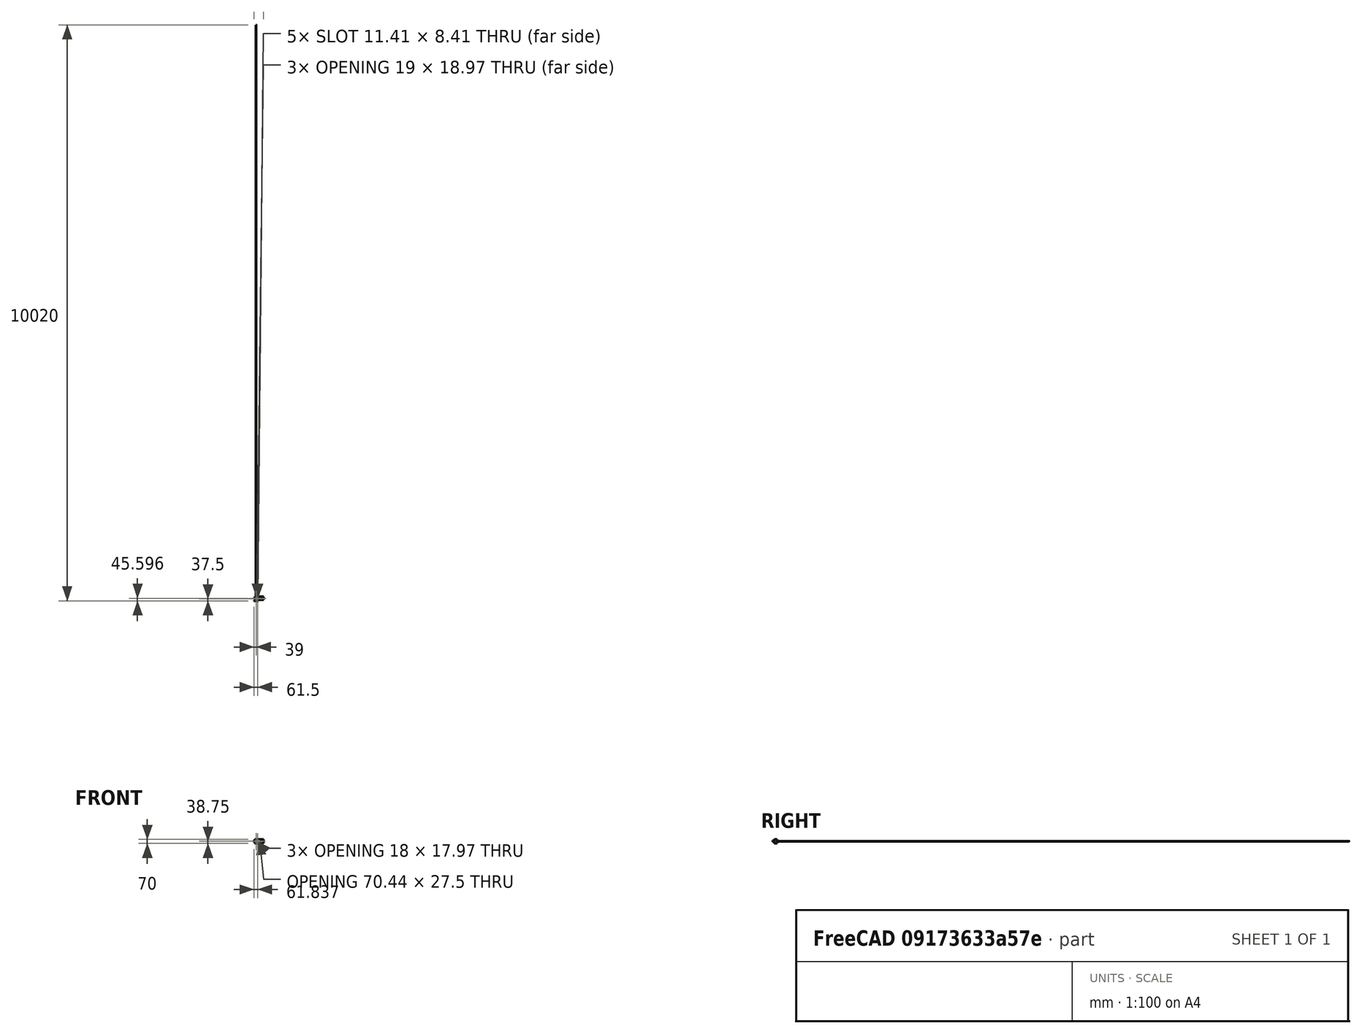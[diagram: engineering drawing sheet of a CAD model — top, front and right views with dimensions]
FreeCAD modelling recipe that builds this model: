
FCSTD DOCUMENT  (FreeCAD 0.16R5861 (Git))
Label: flexystruder_body_holderV0.3
License: CreativeCommons Attribution-ShareAlike
LicenseURL: http://creativecommons.org/licenses/by-sa/4.0/
objects: Sketcher::SketchObject×8, PartDesign::Pad×6, Part::Feature×4, PartDesign::Pocket×2, Mesh::Feature×1, PartDesign::Chamfer×1, Part::Cut×1, PartDesign::Fillet×1
note: 31 computed .brp shape members not serialized (recipe doc carries the construction recipe); baked Part::Feature solids carry a one-line shape summary decoded from their .brp

FEATURE [Mesh::Feature] flexystruder_body_hex_v2_0  label="flexystruder_body_hex_v2.0"
FEATURE [Part::Feature] flexystruder_body_hex_v2_0001
  shape: bbox 97.06 x 64.55 x 27.5 mm, 7934 faces, 0 solids (baked)
FEATURE [Part::Feature] flexystruder_body_hex_v2_0001001  label="flexystruder_body_hex_v2_0002"
  shape: bbox 97.06 x 64.55 x 27.5 mm, 4378 faces, 0 solids (baked)
FEATURE [Part::Feature] flexystruder_body_hex_v2_0001001_solid  label="flexystruder_body_hex_v2_0002 (Solid)"
  shape: bbox 97.06 x 64.55 x 27.5 mm, 4378 faces (baked)
FEATURE [Sketcher::SketchObject] Sketch
  Placement = pos=(0,0,0) rot=(1,0,0;3.14159rad)
  Support = -> flexystruder_body_hex_v2_0001001_solid [Face1922]
  sketch-geometry (17):
    g0: ArcOfCircle CenterX=28 CenterY=-45.596 CenterZ=0 NormalX=0 NormalY=0 NormalZ=1 Radius=4.20615 StartAngle=4.71239 EndAngle=7.85398
    g1: ArcOfCircle CenterX=25 CenterY=-45.596 CenterZ=0 NormalX=0 NormalY=0 NormalZ=1 Radius=4.20615 StartAngle=1.5708 EndAngle=4.71239
    g2: LineSegment StartX=28 StartY=-41.3899 StartZ=0 EndX=25 EndY=-41.3899 EndZ=0
    g3: LineSegment StartX=28 StartY=-49.8022 StartZ=0 EndX=25 EndY=-49.8022 EndZ=0
    g4: ArcOfCircle CenterX=52.7327 CenterY=-58.2604 CenterZ=0 NormalX=0 NormalY=0 NormalZ=1 Radius=4.37439 StartAngle=1.5708 EndAngle=4.71239
    g5: ArcOfCircle CenterX=55.547 CenterY=-58.2604 CenterZ=0 NormalX=0 NormalY=0 NormalZ=1 Radius=4.37439 StartAngle=4.71239 EndAngle=7.85398
    g6: LineSegment StartX=52.7327 StartY=-62.6347 StartZ=0 EndX=55.547 EndY=-62.6347 EndZ=0
    g7: LineSegment StartX=52.7327 StartY=-53.886 StartZ=0 EndX=55.547 EndY=-53.886 EndZ=0
    g8: ArcOfCircle CenterX=41 CenterY=-17.6915 CenterZ=0 NormalX=0 NormalY=0 NormalZ=1 Radius=4.05397 StartAngle=4.71239 EndAngle=7.85398
    g9: ArcOfCircle CenterX=37.752 CenterY=-17.6915 CenterZ=0 NormalX=0 NormalY=0 NormalZ=1 Radius=4.05397 StartAngle=1.5708 EndAngle=4.71239
    g10: LineSegment StartX=41 StartY=-13.6375 StartZ=0 EndX=37.752 EndY=-13.6375 EndZ=0
    g11: LineSegment StartX=41 StartY=-21.7455 StartZ=0 EndX=37.752 EndY=-21.7455 EndZ=0
    g12: LineSegment StartX=23.6875 StartY=-6 StartZ=0 EndX=35.6731 EndY=-6 EndZ=0
    g13: LineSegment StartX=16.4026 StartY=-28 StartZ=0 EndX=28.3058 EndY=-28 EndZ=0
    g14: LineSegment StartX=28.3058 StartY=-28 StartZ=0 EndX=35.6731 EndY=-6 EndZ=0
    g15: LineSegment StartX=16.4026 StartY=-28 StartZ=0 EndX=16.4026 EndY=-12.5849 EndZ=0
    g16: ArcOfCircle CenterX=23.5917 CenterY=-13.2161 CenterZ=0 NormalX=0 NormalY=0 NormalZ=1 Radius=7.21677 StartAngle=1.55753 EndAngle=3.05401
  constraints (26):
    c: Tangent(g0,g3) = 1.5708
    c: Tangent(g0,g2) = -1.5708
    c: Tangent(g2,g1) = -1.5708
    c: Tangent(g3,g1) = 1.5708
    c: Horizontal(g2)
    c: Equal(g0,g1)
    c: Tangent(g4,g7) = 1.5708
    c: Tangent(g4,g6) = -1.5708
    c: Tangent(g6,g5) = -1.5708
    c: Tangent(g7,g5) = 1.5708
    c: Horizontal(g6)
    c: Equal(g4,g5)
    c: Tangent(g8,g11) = 1.5708
    c: Tangent(g8,g10) = -1.5708
    c: Tangent(g10,g9) = -1.5708
    c: Tangent(g11,g9) = 1.5708
    c: Horizontal(g10)
    c: Equal(g8,g9)
    c: Horizontal(g12)
    c: Horizontal(g13)
    c: Coincident(g14,g13)
    c: Coincident(g14,g12)
    c: Coincident(g15,g13)
    c: Vertical(g15)
    c: Coincident(g16,g12)
    c: Coincident(g16,g15)
FEATURE [PartDesign::Pad] Pad
  Length = 9.5
  Length2 = 100
  Reversed = true
  Sketch = -> Sketch
  Type = 0
FEATURE [Sketcher::SketchObject] Sketch001
  ExternalGeometry = -> [Pad]
  Placement = pos=(17.5,0,0) rot=(0.57735,0.57735,0.57735;2.0944rad)
  Support = -> Pad [Face375]
  sketch-geometry (4):
    g0: LineSegment StartX=26.5 StartY=12.5 StartZ=0 EndX=17.6702 EndY=12.5 EndZ=0
    g1: LineSegment StartX=17.6702 StartY=12.5 StartZ=0 EndX=17.6702 EndY=9.5 EndZ=0
    g2: LineSegment StartX=17.6702 StartY=9.5 StartZ=0 EndX=26.5 EndY=9.5 EndZ=0
    g3: LineSegment StartX=26.5 StartY=9.5 StartZ=0 EndX=26.5 EndY=12.5 EndZ=0
  constraints (10):
    c: Coincident(g0,g1)
    c: Coincident(g1,g2)
    c: Coincident(g2,g3)
    c: Coincident(g3,g0)
    c: Horizontal(g0)
    c: Horizontal(g2)
    c: Vertical(g1)
    c: Vertical(g3)
    c: Coincident(g0,g-4)
    c: PointOnObject(g1,g-3)
FEATURE [PartDesign::Pad] Pad001
  Length = 3
  Length2 = 100
  Sketch = -> Sketch001
  Type = 0
FEATURE [PartDesign::Chamfer] Chamfer
  Base = -> Pad001 [Edge1475]
  Size = 2.9
FEATURE [Sketcher::SketchObject] Sketch002
  ExternalGeometry = -> [Chamfer]
  Placement = pos=(0,0,27.5) rot=(0,0,1;0rad)
  Support = -> Chamfer [Face24]
  sketch-geometry (4):
    g0: LineSegment StartX=-6.5 StartY=48.2121 StartZ=0 EndX=-6.5 EndY=27.0119 EndZ=0
    g1: ArcOfCircle CenterX=3.84323 CenterY=38.0759 CenterZ=0 NormalX=0 NormalY=0 NormalZ=1 Radius=14.4819 StartAngle=0.364009 EndAngle=2.3663
    g2: LineSegment StartX=17.3762 StartY=43.2318 StartZ=0 EndX=17.5 EndY=37.4236 EndZ=0
    g3: ArcOfCircle CenterX=3.40646 CenterY=37.0436 CenterZ=0 NormalX=0 NormalY=0 NormalZ=1 Radius=14.0987 StartAngle=3.93327 EndAngle=6.31015
  constraints (10):
    c: Vertical(g0)
    c: Coincident(g0,g-5)
    c: Coincident(g0,g-6)
    c: Coincident(g1,g0)
    c: Coincident(g1,g-9)
    c: PointOnObject(g-21,g1)
    c: Coincident(g2,g1)
    c: Coincident(g2,g-7)
    c: Coincident(g3,g0)
    c: Coincident(g3,g2)
FEATURE [PartDesign::Pad] Pad002
  Length = 10
  Length2 = 100
  Reversed = true
  Sketch = -> Sketch002
  Type = 3
  UpToFace = -> Chamfer [Face709]
FEATURE [Sketcher::SketchObject] Sketch003
  ExternalGeometry = -> [Pad002]
  Placement = pos=(0,0,0) rot=(1,0,0;3.14159rad)
  Support = -> Pad002 [Face634]
  sketch-geometry (4):
    g0: LineSegment StartX=62.0584 StartY=-58.2729 StartZ=0 EndX=17.5 EndY=-58.2729 EndZ=0
    g1: LineSegment StartX=17.5 StartY=-58.2729 StartZ=0 EndX=17.5 EndY=-17.6702 EndZ=0
    g2: LineSegment StartX=17.5 StartY=-17.6702 StartZ=0 EndX=62.0584 EndY=-17.6702 EndZ=0
    g3: LineSegment StartX=62.0584 StartY=-17.6702 StartZ=0 EndX=62.0584 EndY=-58.2729 EndZ=0
  constraints (10):
    c: Coincident(g0,g1)
    c: Coincident(g1,g2)
    c: Coincident(g2,g3)
    c: Coincident(g3,g0)
    c: Horizontal(g0)
    c: Horizontal(g2)
    c: Vertical(g1)
    c: Vertical(g3)
    c: Coincident(g0,g-3)
    c: Coincident(g1,g-4)
FEATURE [PartDesign::Pad] Pad003
  Length = 9.5
  Length2 = 100
  Reversed = true
  Sketch = -> Sketch003
  Type = 0
FEATURE [Sketcher::SketchObject] Sketch004
  ExternalGeometry = -> [Pad003]
  Placement = pos=(0,0,0) rot=(1,0,0;3.14159rad)
  Support = -> Pad003 [Face456]
  sketch-geometry (4):
    g0: LineSegment StartX=16.4026 StartY=-12.5849 StartZ=0 EndX=-6.5 EndY=-12.5849 EndZ=0
    g1: LineSegment StartX=-6.5 StartY=-12.5849 StartZ=0 EndX=-6.5 EndY=-27.0119 EndZ=0
    g2: LineSegment StartX=-6.5 StartY=-27.0119 StartZ=0 EndX=16.4026 EndY=-27.0119 EndZ=0
    g3: LineSegment StartX=16.4026 StartY=-27.0119 StartZ=0 EndX=16.4026 EndY=-12.5849 EndZ=0
  constraints (10):
    c: Coincident(g0,g1)
    c: Coincident(g1,g2)
    c: Coincident(g2,g3)
    c: Coincident(g3,g0)
    c: Horizontal(g0)
    c: Horizontal(g2)
    c: Vertical(g1)
    c: Vertical(g3)
    c: Coincident(g0,g-4)
    c: Coincident(g1,g-3)
FEATURE [PartDesign::Pad] Pad004
  Length = 1
  Length2 = 100
  Reversed = true
  Sketch = -> Sketch004
  Type = 0
FEATURE [Part::Feature] Pad004001  label="Pad005"
  shape: bbox 97.06 x 64.55 x 27.5 mm, 2094 faces (baked)
FEATURE [Sketcher::SketchObject] Sketch005
  Placement = pos=(0,0,0) rot=(0.57735,0.57735,0.57735;2.0944rad)
  sketch-geometry (4):
    g0: LineSegment StartX=20 StartY=45 StartZ=0 EndX=75 EndY=45 EndZ=0
    g1: LineSegment StartX=75 StartY=45 StartZ=0 EndX=75 EndY=-25 EndZ=0
    g2: LineSegment StartX=75 StartY=-25 StartZ=0 EndX=20 EndY=-25 EndZ=0
    g3: LineSegment StartX=20 StartY=-25 StartZ=0 EndX=20 EndY=45 EndZ=0
  constraints (12):
    c: Coincident(g0,g1)
    c: Coincident(g1,g2)
    c: Coincident(g2,g3)
    c: Coincident(g3,g0)
    c: Horizontal(g0)
    c: Horizontal(g2)
    c: Vertical(g1)
    c: Vertical(g3)
    c: DistanceY(g1) = -70
    c: DistanceY(g-1,g2) = -25
    c: DistanceX(g-1,g1) = 75
    c: DistanceX(g2) = -55
FEATURE [PartDesign::Pad] Pad004002
  Length = 130
  Length2 = 20
  Placement = pos=(0,0,0) rot=(0.57735,0.57735,0.57735;2.0944rad)
  Sketch = -> Sketch005
  Type = 4
FEATURE [Part::Cut] Cut
  Base = -> Pad004002
  Tool = -> Pad004001
FEATURE [Sketcher::SketchObject] Sketch006
  ExternalGeometry = -> [Cut]
  Placement = pos=(0,0,45) rot=(0,0,1;0rad)
  Support = -> Cut [Face1]
  sketch-geometry (3):
    g0: ArcOfCircle CenterX=66.7062 CenterY=83.914 CenterZ=0 NormalX=0 NormalY=0 NormalZ=1 Radius=63.9184 StartAngle=4.72413 EndAngle=6.14327
    g1: LineSegment StartX=130 StartY=75 StartZ=0 EndX=130 EndY=20 EndZ=0
    g2: LineSegment StartX=130 StartY=20 StartZ=0 EndX=67.4569 EndY=20 EndZ=0
  constraints (8):
    c: Coincident(g1,g0)
    c: Coincident(g1,g-4)
    c: Vertical(g1)
    c: Coincident(g2,g1)
    c: Coincident(g2,g0)
    c: Horizontal(g2)
    c: Coincident(g0,g-3)
    c: Coincident(g1,g-3)
FEATURE [PartDesign::Pocket] Pocket
  Length = 5
  Sketch = -> Sketch006
  Type = 1
FEATURE [PartDesign::Fillet] Fillet
  Base = -> Pocket [Edge3,Edge4,Edge1,Edge7,Edge6,Edge10,Edge12]
  Radius = 10
FEATURE [Sketcher::SketchObject] Sketch007
  Placement = pos=(0,20,0) rot=(1,0,0;1.5708rad)
  Support = -> Fillet [Face12]
  sketch-geometry (1):
    g0: Circle CenterX=0.551868 CenterY=14.0293 CenterZ=0 NormalX=0 NormalY=0 NormalZ=1 Radius=4
  constraints (1):
    c: Radius(g0) = 4
FEATURE [PartDesign::Pocket] Pocket001
  Length = 5
  Sketch = -> Sketch007
  Type = 1
